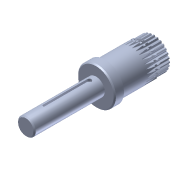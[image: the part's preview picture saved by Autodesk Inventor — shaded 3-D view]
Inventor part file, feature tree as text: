
AUTODESK INVENTOR PART (.ipt)
format: ipt  version: 2013 (Build 170138000, 138)  size: 1,411,072 bytes
history: native  units: in
note: dims shown in document units (in); Inventor stores cm internally (conversion verified against a paired STEP export)
features: other x2, imported_body x2, chamfer x1
ambient origin geometry x8: Origin, YZ Plane, XZ Plane, XY Plane, X Axis, Y Axis, Z Axis, Center Point
feature tree (5):
  other  "8MM CIM SHAFT"
  other  "217-2625-022 Rev11"
  chamfer  "Chamfer3"  [1 undecoded]
  imported_body  "Base1"
  imported_body  "Base2"
note: 1 required parameter value undecoded (feature->parameter linkage not recoverable at this tier; creation-order binding heuristic only, values carry confidence <= 0.55)
